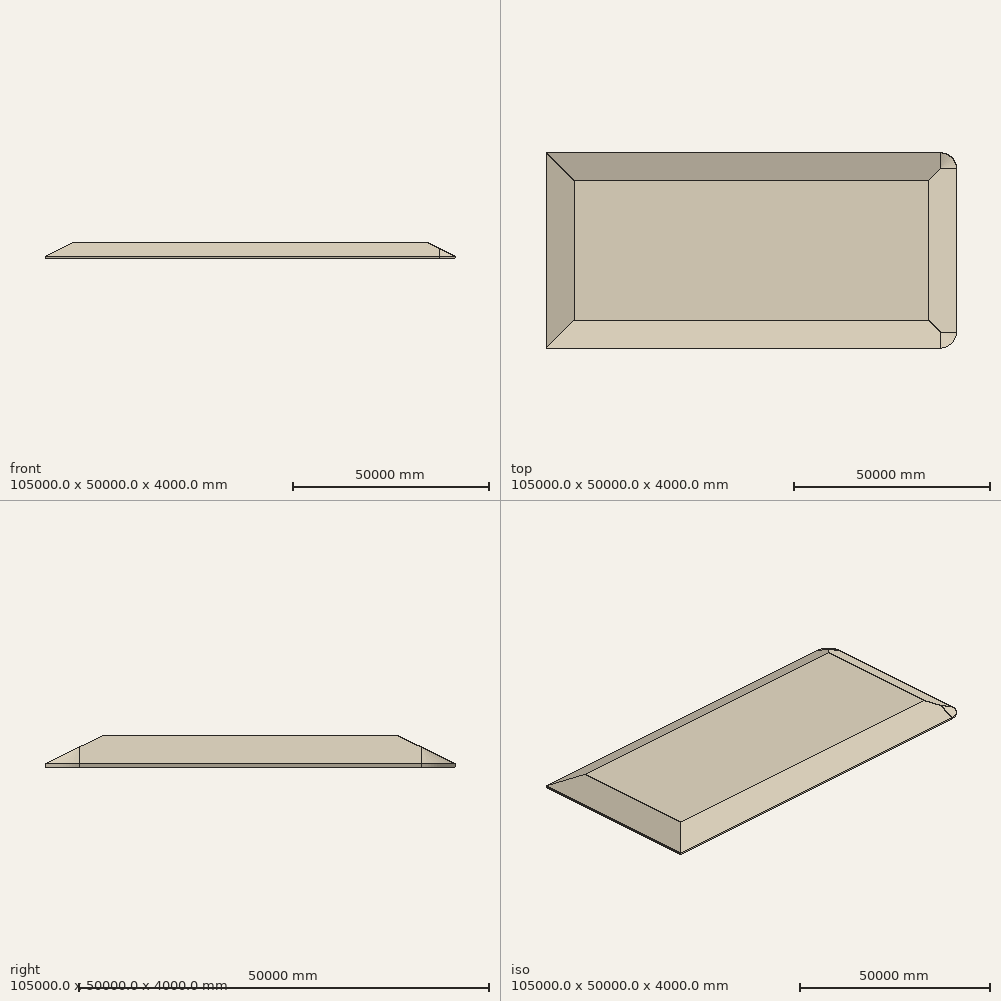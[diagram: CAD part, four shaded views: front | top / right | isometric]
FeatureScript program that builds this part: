
annotation { "Feature Type Name" : "Feature", "Feature Type Description" : "" }
export const myFeature = defineFeature(function(context is Context, id is Id, definition is map)
    precondition{}
    {
        {
            var Q0;
            Q0=qCreatedBy(makeId("Top.planeOp"),FACE);
            var sketch = newSketch(context, id + "F0", { "sketchPlane" : qUnion([Q0])});
            skLineSegment(sketch, "E0.bottom", {"start": v(-104948.3, 54055.58) * mm, "end": v(-4048.3, 54055.58) * mm});
            skLineSegment(sketch, "E0.top", {"start": v(-104948.3, 4055.58) * mm, "end": v(-4048.3, 4055.58) * mm});
            skLineSegment(sketch, "E0.left", {"start": v(-104948.3, 54055.58) * mm, "end": v(-104948.3, 4055.58) * mm});
            skLineSegment(sketch, "E0.right", {"start": v(51.7, 49955.58) * mm, "end": v(51.7, 8155.58) * mm});
            skPoint(sketch, "E1.visualSharp", {"position": v(-104948.3, 54055.58) * mm});
            skLineSegment(sketch, "E1.filletArc", {"start": v(-104948.3, 54055.58) * mm, "end": v(-104948.3, 54055.58) * mm});
            skPoint(sketch, "E2.visualSharp", {"position": v(-104948.3, 4055.58) * mm});
            skLineSegment(sketch, "E2.filletArc", {"start": v(-104948.3, 4055.58) * mm, "end": v(-104948.3, 4055.58) * mm});
            skPoint(sketch, "E3.visualSharp", {"position": v(51.7, 4055.58) * mm});
            skArc(sketch, "E3.filletArc", {"start": v(-4048.3, 4055.58) * mm, "mid": v(-1149.15, 5256.44) * mm, "end": v(51.7, 8155.58) * mm});
            skPoint(sketch, "E4.visualSharp", {"position": v(51.7, 54055.58) * mm});
            skArc(sketch, "E4.filletArc", {"start": v(51.7, 49955.58) * mm, "mid": v(-1149.15, 52854.72) * mm, "end": v(-4048.3, 54055.58) * mm});
            skSolve(sketch);
        }
        {
            var Q0;
            Q0=makeQuery(id+"F0.imprint","IMPRINT",FACE,{"disambiguationData":[TD([[makeQuery(id+"F0.imprint","IMPRINT",EDGE,{"derivedFrom":sQuery(id+"F0.wireOp",EDGE,"E0.bottom")}),-1.0]])]});
            extrude(context, id + "F1", {"entities" : qUnion([Q0]), "depth" : 3500 * mm, "hasDraft" : true, "draftAngle" : 64 * degree, "draftPullDirection" : true});
        }
        {
            var Q0;
            Q0=makeQuery(id+"F1.opExtrude","CAP_FACE",FACE,{"disambiguationData":[OSD([sQuery(id+"F0.wireOp",EDGE,"E0.bottom"),sQuery(id+"F0.wireOp",EDGE,"E0.top"),sQuery(id+"F0.wireOp",EDGE,"E0.left"),sQuery(id+"F0.wireOp",EDGE,"E0.right"),sQuery(id+"F0.wireOp",EDGE,"E1.filletArc"),sQuery(id+"F0.wireOp",EDGE,"E2.filletArc"),sQuery(id+"F0.wireOp",EDGE,"E3.filletArc"),sQuery(id+"F0.wireOp",EDGE,"E4.filletArc")])],"isStart":true});
            extrude(context, id + "F2", {"entities" : qUnion([Q0]), "operationType" : NewBodyOperationType.ADD, "depth" : 500 * mm});
        }
    });
